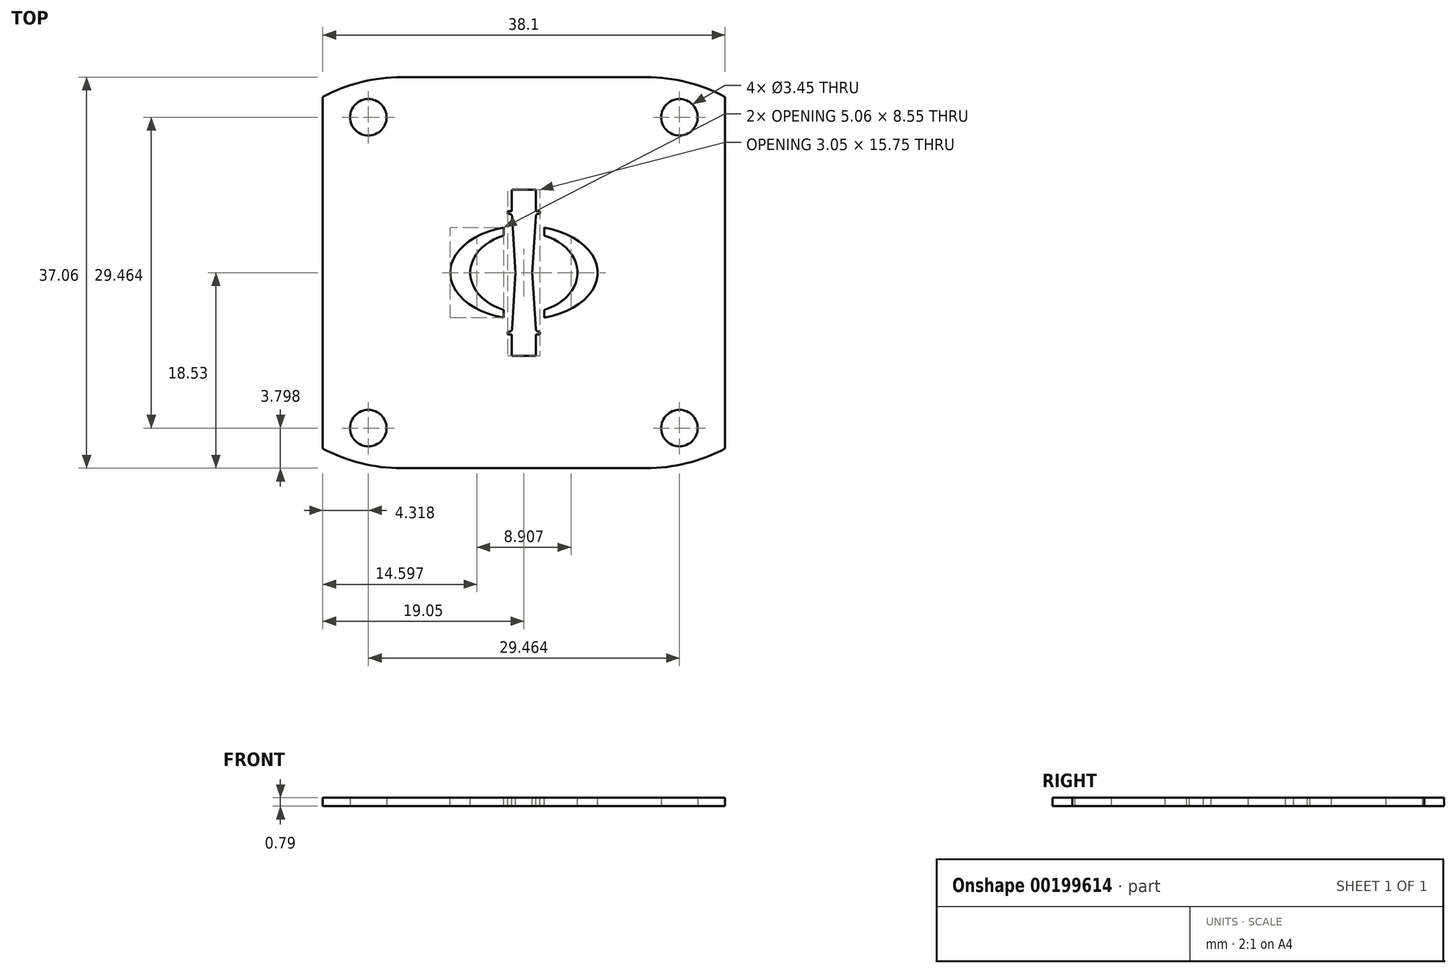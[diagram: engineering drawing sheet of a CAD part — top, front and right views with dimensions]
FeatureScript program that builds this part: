
annotation { "Feature Type Name" : "Feature", "Feature Type Description" : "" }
export const myFeature = defineFeature(function(context is Context, id is Id, definition is map)
    precondition{}
    {
        {
            var Q0;
            Q0=qCreatedBy(makeId("Top.planeOp"),FACE);
            var sketch = newSketch(context, id + "F0", { "sketchPlane" : qUnion([Q0])});
            skLineSegment(sketch, "E0", {"start": v(-19.05, 0) * mm, "end": v(-19.05, 16.67) * mm});
            skLineSegment(sketch, "E1", {"start": v(19.05, 0) * mm, "end": v(19.05, 16.67) * mm});
            skArc(sketch, "E2", {"start": v(-11.58, 18.53) * mm, "mid": v(-15.43, 18.06) * mm, "end": v(-19.05, 16.67) * mm});
            skArc(sketch, "E3", {"start": v(19.05, 16.67) * mm, "mid": v(15.43, 18.06) * mm, "end": v(11.58, 18.53) * mm});
            skLineSegment(sketch, "E4", {"start": v(-11.58, 18.53) * mm, "end": v(0, 18.53) * mm});
            skLineSegment(sketch, "E5", {"start": v(0, 18.53) * mm, "end": v(11.58, 18.53) * mm});
            skLineSegment(sketch, "E6", {"start": v(-39.62, 0) * mm, "end": v(36.58, 0) * mm, "construction": true});
            skLineSegment(sketch, "E7.MirrorCS", {"start": v(-19.05, 0) * mm, "end": v(-19.05, -16.67) * mm});
            skLineSegment(sketch, "E8.MirrorCS", {"start": v(19.05, 0) * mm, "end": v(19.05, -16.67) * mm});
            skLineSegment(sketch, "E9.MirrorCS", {"start": v(-11.58, -18.53) * mm, "end": v(0, -18.53) * mm});
            skLineSegment(sketch, "E10.MirrorCS", {"start": v(0, -18.53) * mm, "end": v(11.58, -18.53) * mm});
            skArc(sketch, "E11.MirrorCS", {"start": v(-11.58, -18.53) * mm, "mid": v(-15.43, -18.06) * mm, "end": v(-19.05, -16.67) * mm});
            skArc(sketch, "E12.MirrorCS", {"start": v(19.05, -16.67) * mm, "mid": v(15.43, -18.06) * mm, "end": v(11.58, -18.53) * mm});
            skCircle(sketch, "E13", {"center": v(-14.73, 14.73) * mm, "radius": 1.73 * mm});
            skCircle(sketch, "E14.MirrorC", {"center": v(-14.73, -14.73) * mm, "radius": 1.73 * mm});
            skLineSegment(sketch, "E15", {"start": v(0, 16.68) * mm, "end": v(0, -10.48) * mm, "construction": true});
            skCircle(sketch, "E16.MirrorC", {"center": v(14.73, 14.73) * mm, "radius": 1.73 * mm});
            skCircle(sketch, "E17.MirrorC", {"center": v(14.73, -14.73) * mm, "radius": 1.73 * mm});
            skSolve(sketch);
        }
        {
            var Q0;
            Q0=qSketchRegion(id+"F0",true);
            extrude(context, id + "F1", {"entities" : qUnion([Q0]), "depth" : 0.8 * mm});
        }
        {
            var Q0;
            Q0=makeQuery(id+"F1.opExtrude","CAP_FACE",FACE,{"disambiguationData":[OSD([sQuery(id+"F0.wireOp",EDGE,"E0"),sQuery(id+"F0.wireOp",EDGE,"E1"),sQuery(id+"F0.wireOp",EDGE,"E2"),sQuery(id+"F0.wireOp",EDGE,"E3"),sQuery(id+"F0.wireOp",EDGE,"E4"),sQuery(id+"F0.wireOp",EDGE,"E5"),sQuery(id+"F0.wireOp",EDGE,"E7.MirrorCS"),sQuery(id+"F0.wireOp",EDGE,"E8.MirrorCS"),sQuery(id+"F0.wireOp",EDGE,"E9.MirrorCS"),sQuery(id+"F0.wireOp",EDGE,"E10.MirrorCS"),sQuery(id+"F0.wireOp",EDGE,"E11.MirrorCS"),sQuery(id+"F0.wireOp",EDGE,"E12.MirrorCS"),sQuery(id+"F0.wireOp",EDGE,"E14.MirrorC"),sQuery(id+"F0.wireOp",EDGE,"E13"),sQuery(id+"F0.wireOp",EDGE,"E16.MirrorC"),sQuery(id+"F0.wireOp",EDGE,"E17.MirrorC")])],"isStart":false});
            var sketch = newSketch(context, id + "F2", { "sketchPlane" : qUnion([Q0])});
            skLineSegment(sketch, "E18", {"start": v(-1.52, -5.59) * mm, "end": v(-1.52, -5.84) * mm});
            skLineSegment(sketch, "E19", {"start": v(-1.14, -5.84) * mm, "end": v(-1.14, -7.87) * mm});
            skLineSegment(sketch, "E20", {"start": v(-1.14, -7.87) * mm, "end": v(0, -7.87) * mm});
            skLineSegment(sketch, "E21", {"start": v(-1.13, -5.35) * mm, "end": v(-0.8, 0) * mm});
            skLineSegment(sketch, "E22", {"start": v(-1.52, -5.59) * mm, "end": v(-1.38, -5.59) * mm});
            skLineSegment(sketch, "E23", {"start": v(-1.52, -5.84) * mm, "end": v(-1.14, -5.84) * mm});
            skPoint(sketch, "E24.visualSharp", {"position": v(-1.14, -5.59) * mm});
            skArc(sketch, "E24.filletArc", {"start": v(-1.38, -5.59) * mm, "mid": v(-1.2, -5.52) * mm, "end": v(-1.13, -5.35) * mm});
            skLineSegment(sketch, "E25", {"start": v(0, 2.97) * mm, "end": v(0, -3.47) * mm, "construction": true});
            skLineSegment(sketch, "E26", {"start": v(3.14, 0) * mm, "end": v(-4.12, 0) * mm, "construction": true});
            skLineSegment(sketch, "E27.MirrorCS", {"start": v(1.52, -5.59) * mm, "end": v(1.38, -5.59) * mm});
            skLineSegment(sketch, "E28.MirrorCS", {"start": v(1.52, -5.84) * mm, "end": v(1.14, -5.84) * mm});
            skArc(sketch, "E29.MirrorCS", {"start": v(1.38, -5.59) * mm, "mid": v(1.2, -5.52) * mm, "end": v(1.13, -5.35) * mm});
            skLineSegment(sketch, "E30.MirrorCS", {"start": v(1.52, -5.59) * mm, "end": v(1.52, -5.84) * mm});
            skLineSegment(sketch, "E31.MirrorCS", {"start": v(-3.14, 0) * mm, "end": v(4.12, 0) * mm, "construction": true});
            skLineSegment(sketch, "E32.MirrorCS", {"start": v(1.13, -5.35) * mm, "end": v(0.8, 0) * mm});
            skPoint(sketch, "E33.MirrorP", {"position": v(1.14, -5.59) * mm});
            skLineSegment(sketch, "E34.MirrorCS", {"start": v(1.14, -7.87) * mm, "end": v(0, -7.87) * mm});
            skLineSegment(sketch, "E35.MirrorCS", {"start": v(1.14, -5.84) * mm, "end": v(1.14, -7.87) * mm});
            skLineSegment(sketch, "E36.MirrorCS", {"start": v(1.52, 5.59) * mm, "end": v(1.38, 5.59) * mm});
            skLineSegment(sketch, "E37.MirrorCS", {"start": v(1.52, 5.59) * mm, "end": v(1.52, 5.84) * mm});
            skLineSegment(sketch, "E38.MirrorCS", {"start": v(-1.52, 5.59) * mm, "end": v(-1.38, 5.59) * mm});
            skLineSegment(sketch, "E39.MirrorCS", {"start": v(-1.52, 5.59) * mm, "end": v(-1.52, 5.84) * mm});
            skArc(sketch, "E40.MirrorCS", {"start": v(-1.38, 5.59) * mm, "mid": v(-1.2, 5.52) * mm, "end": v(-1.13, 5.35) * mm});
            skLineSegment(sketch, "E41.MirrorCS", {"start": v(1.52, 5.84) * mm, "end": v(1.14, 5.84) * mm});
            skArc(sketch, "E42.MirrorCS", {"start": v(1.38, 5.59) * mm, "mid": v(1.2, 5.52) * mm, "end": v(1.13, 5.35) * mm});
            skLineSegment(sketch, "E43.MirrorCS", {"start": v(-1.52, 5.84) * mm, "end": v(-1.14, 5.84) * mm});
            skLineSegment(sketch, "E44.MirrorCS", {"start": v(1.14, 5.84) * mm, "end": v(1.14, 7.87) * mm});
            skLineSegment(sketch, "E45.MirrorCS", {"start": v(-1.13, 5.35) * mm, "end": v(-0.8, 0) * mm});
            skLineSegment(sketch, "E46.MirrorCS", {"start": v(-1.14, 7.87) * mm, "end": v(0, 7.87) * mm});
            skLineSegment(sketch, "E47.MirrorCS", {"start": v(1.14, 7.87) * mm, "end": v(0, 7.87) * mm});
            skPoint(sketch, "E48.MirrorP", {"position": v(1.14, 5.59) * mm});
            skLineSegment(sketch, "E49.MirrorCS", {"start": v(-1.14, 5.84) * mm, "end": v(-1.14, 7.87) * mm});
            skPoint(sketch, "E50.MirrorP", {"position": v(-1.14, 5.59) * mm});
            skLineSegment(sketch, "E51.MirrorCS", {"start": v(1.13, 5.35) * mm, "end": v(0.8, 0) * mm});
            skEllipticalArc(sketch, "E52", {});
            skEllipticalArc(sketch, "E53", {});
            skLineSegment(sketch, "E54", {"start": v(1.92, 3.53) * mm, "end": v(1.92, 4.27) * mm});
            skLineSegment(sketch, "E55.MirrorCS", {"start": v(1.92, -3.53) * mm, "end": v(1.92, -4.27) * mm});
            skLineSegment(sketch, "E56.MirrorCS", {"start": v(-1.92, 3.53) * mm, "end": v(-1.92, 4.27) * mm});
            skLineSegment(sketch, "E57.MirrorCS", {"start": v(-1.92, -3.53) * mm, "end": v(-1.92, -4.27) * mm});
            skEllipticalArc(sketch, "E58.trimOffspring", {});
            skEllipticalArc(sketch, "E59.trimOffspring", {});
            const initialGuessF2  = {"E52": [0, 0, 1, 0, 0.00508, 0.00381, 1.9588299419890658, 4.32435536519052], "E53": [0, 0, 1, 0, 0.006985, 0.004445, 1.8495705701853444, 4.433614736994242], "E58.trimOffspring": [0, 0, 1, 0, 0.00508, 0.00381, 5.100422595578859, 1.1827627116007275], "E59.trimOffspring": [0, 0, 1, 0, 0.006985, 0.004445, 4.991163223775137, 1.2920220834044487]};
            skSetInitialGuess(sketch, initialGuessF2);
            skSolve(sketch);
        }
        {
            var Q0;
            Q0=makeQuery(id+"F2.imprint","IMPRINT",FACE,{"disambiguationData":[TD([[makeQuery(id+"F2.imprint","IMPRINT",EDGE,{"derivedFrom":sQuery(id+"F2.wireOp",EDGE,"e244e818-81d2-465f-a15c-6a6496128eca1.MirrorCS")}),1.0]])]});
            var Q1;
            Q1=makeQuery(id+"F2.imprint","IMPRINT",FACE,{"disambiguationData":[TD([[makeQuery(id+"F2.imprint","IMPRINT",EDGE,{"derivedFrom":sQuery(id+"F2.wireOp",EDGE,"E18")}),1.0]])]});
            var Q2;
            Q2=makeQuery(id+"F2.imprint","IMPRINT",FACE,{"disambiguationData":[TD([[makeQuery(id+"F2.imprint","IMPRINT",EDGE,{"derivedFrom":sQuery(id+"F2.wireOp",EDGE,"ty6V3Qsz-AUhm-mqbV-rWOf-qFsxb7qC91Gp")}),1.0]])]});
            var Q3;
            Q3=makeQuery(id+"F2.imprint","IMPRINT",FACE,{"disambiguationData":[TD([[makeQuery(id+"F2.imprint","IMPRINT",EDGE,{"derivedFrom":sQuery(id+"F2.wireOp",EDGE,"b3311bc9-47f5-4ebc-a715-56fcb5429c292.MirrorCS")}),1.0]])]});
            var Q4;
            Q4=makeQuery(id+"F2.imprint","IMPRINT",FACE,{"disambiguationData":[TD([[makeQuery(id+"F2.imprint","IMPRINT",EDGE,{"derivedFrom":sQuery(id+"F2.wireOp",EDGE,"cc02e8ae-c0aa-40ef-9190-e4cb289d595d6.MirrorCS")}),1.0]])]});
            var Q5;
            Q5=makeQuery(id+"F2.imprint","IMPRINT",FACE,{"disambiguationData":[TD([[makeQuery(id+"F2.imprint","IMPRINT",EDGE,{"derivedFrom":sQuery(id+"F2.wireOp",EDGE,"9c620a25-0ec8-4a03-813b-536c0122b8750.MirrorCS")}),-1.0]])]});
            var Q6;
            Q6=makeQuery(id+"F2.imprint","IMPRINT",FACE,{"disambiguationData":[TD([[makeQuery(id+"F2.imprint","IMPRINT",EDGE,{"derivedFrom":sQuery(id+"F2.wireOp",EDGE,"8CR0XLE6-VZYH-Vc5D-PsDY-LuH6upcb9dxB")}),-1.0]])]});
            var Q7;
            Q7=makeQuery(id+"F2.imprint","IMPRINT",FACE,{"disambiguationData":[TD([[makeQuery(id+"F2.imprint","IMPRINT",EDGE,{"derivedFrom":sQuery(id+"F2.wireOp",EDGE,"cc02e8ae-c0aa-40ef-9190-e4cb289d595d3.MirrorCS")}),1.0]])]});
            var Q8;
            Q8=makeQuery(id+"F2.imprint","IMPRINT",FACE,{"disambiguationData":[TD([[makeQuery(id+"F2.imprint","IMPRINT",EDGE,{"derivedFrom":sQuery(id+"F2.wireOp",EDGE,"E52")}),-1.0]])]});
            var Q9;
            Q9=makeQuery(id+"F2.imprint","IMPRINT",FACE,{"disambiguationData":[TD([[makeQuery(id+"F2.imprint","IMPRINT",EDGE,{"derivedFrom":sQuery(id+"F2.wireOp",EDGE,"E54")}),-1.0]])]});
            extrude(context, id + "F3", {"entities" : qUnion([Q0, Q1, Q2, Q3, Q4, Q5, Q6, Q7, Q8, Q9]), "operationType" : NewBodyOperationType.REMOVE, "oppositeDirection" : true, "depth" : 25.4 * mm});
        }
    });
